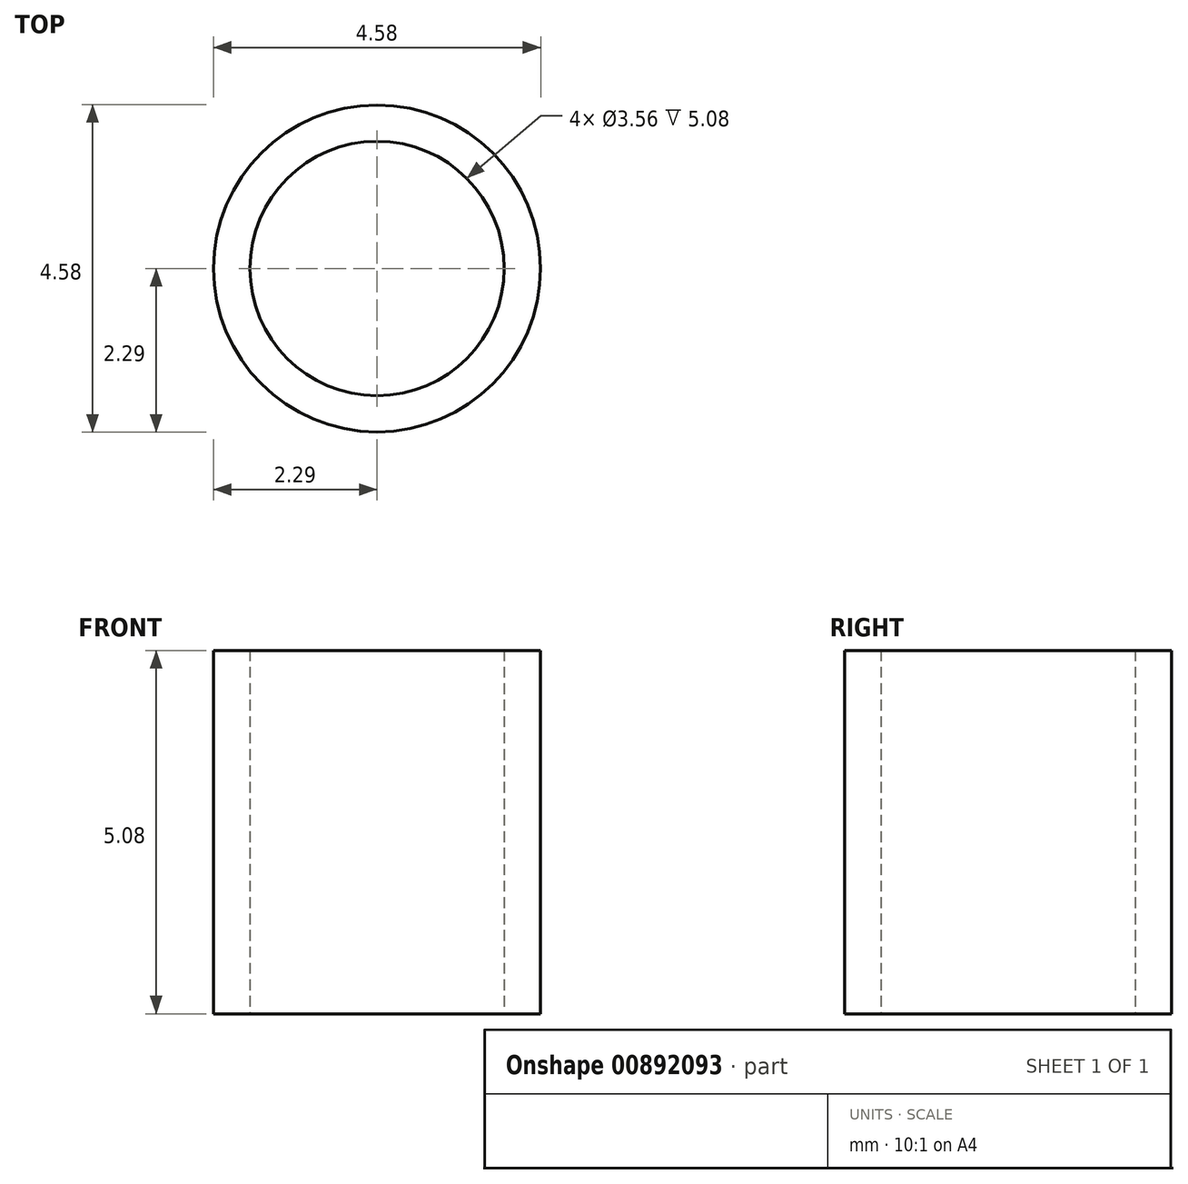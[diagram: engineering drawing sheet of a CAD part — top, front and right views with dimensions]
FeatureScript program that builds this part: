
annotation { "Feature Type Name" : "Feature", "Feature Type Description" : "" }
export const myFeature = defineFeature(function(context is Context, id is Id, definition is map)
    precondition{}
    {
        {
            var Q0;
            Q0=qCreatedBy(makeId("Top.planeOp"),FACE);
            var sketch = newSketch(context, id + "F0", { "sketchPlane" : qUnion([Q0])});
            skCircle(sketch, "E0", {"center": v(0, 0) * mm, "radius": 1.78 * mm});
            skCircle(sketch, "E1", {"center": v(0, 0) * mm, "radius": 2.29 * mm});
            skSolve(sketch);
        }
        {
            var Q0;
            Q0=makeQuery(id+"F0.imprint","IMPRINT",FACE,{"disambiguationData":[TD([[makeQuery(id+"F0.imprint","IMPRINT",EDGE,{"derivedFrom":sQuery(id+"F0.wireOp",EDGE,"E0")}),-1.0]])]});
            extrude(context, id + "F1", {"entities" : qUnion([Q0]), "depth" : 5.08 * mm, "offsetDistance" : 25.4 * mm});
        }
    });
